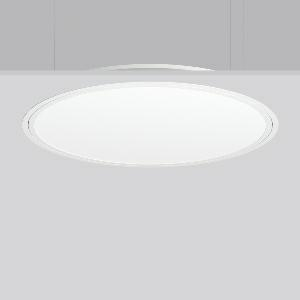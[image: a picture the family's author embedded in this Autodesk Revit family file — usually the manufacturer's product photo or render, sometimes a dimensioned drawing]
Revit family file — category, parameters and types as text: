
# Revit family: triona_round_e_312387_002_1_12_b85f
name_source: partatom
category: Lighting Fixtures
units: mm (PartAtom-declared; Revit-internal decimal feet)

## family parameters
Cut with Voids When Loaded = No
Host = Face
Light Source = No
Part Type = Normal
Room Calculation Point = No
Round Connector Dimension = Use Diameter
Shared = No

## types (1)
- TRIONA round E (1 x LED Modul 840, 8300 lm, 4000)
    Apparent Load = 80 VA
    CIE Flux Codes = 49 80 96 100 100
    Color Rendering = 80
    Color Temperature = 4000
    Default Elevation = 1800 mm
    Description = Series: TRIONA round
Decorative round LED recessed surface luminaire. Cover made of sheet steel, powder-coated. Frame made of aluminium, powder-coated. Recessed ring: aluminium extrusion profile, powder coated. Light emission through a diffuser: plastic, opal. Lightguide and diffuser made of non-yellowing plastic (PMMA). Lateral light emission (RZB SIDELITE technology) for above-average homogeneous light distribution. Suitable for installation in cavity ceilings. Tool-free mounting system thanks to the rocker arm mechanism (patent pending). Electronic ballast included. Very easy installation thanks to Plug+Play connection. 
Colour: traffic white, matt (RAL 9016)
Diameter: 889 mm
Height: 2 mm
Cut-out diameter: 866 mm
Recess height: 100 mm
Luminaire: recess height: 89 mm
Lamp: LED
Socket: without socket
Colour temperature: 4000K
Colour rendering index (CRI): 80
System power: 80 W
Rated luminous flux: 8300 lm
Luminous efficiency: 104 lm/W
Control gear: Converter, dimmable, DALI
Protection class: I
Type of protection: IP 40
    Height = 0 mm  [stored 0 ft]
    Lamp = 1 x LED Modul 840
    Lamp Light Flux = 8300 lm
    Lamp count = 1
    Length = 889 mm
    Lifetime = 50000 h
    Luminous efficacy = 104 lm/W
    Manufacturer = RZB
    ModVariant = No
    Model = 312387.002.1.12
    Mounting Place = Ceiling
    Mounting Type = Recessed
    Number of Poles = 1
    OnlyDefault = Yes
    Power Factor = 1
    Product Name = TRIONA round E
    Product group = Recessed modular luminaires
    ProductGroupID = 406
    Protection Class = Protection class I
    Protection Degree = IP 20
    RLX_Detail_Level = 1
    RLX_Emergency_Light_Flux = 0 lm
    RLX_Emergency_Type = 0
    RLX_Emergency_Type_DB = No
    RlxData = <blob elided: 37825 chars, md5=55655a9e>
    Socket = socket
    Standby Power = 0 W
    System Light Flux = 8300 lm
    System Power = 80 W
    Type Comments = Product without accessories
    Type Image = 312387.002.12.jpg
    URL = http://relux.com
    VarID = ---
    Voltage = 230 V
    Voltage Range = 220-240 V
    Weight = 0.00 kg
    Width = 0 mm  [stored 0 ft]

note: [stored X ft] marks values corroborated as IEEE doubles in the binary element streams (Revit-internal decimal feet)

## geometry (parser evidence)
native form markers: Blend x4, Sweep x11
no freeform markers — native parametric forms only
